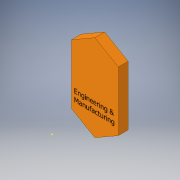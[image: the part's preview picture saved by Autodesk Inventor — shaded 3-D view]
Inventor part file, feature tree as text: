
AUTODESK INVENTOR PART (.ipt)
format: ipt  version: 2018 (Build 220112000, 112)  size: 98,304 bytes
history: native  units: in
note: dims shown in document units (in); Inventor stores cm internally (conversion verified against a paired STEP export)
features: sketch x2, extrude x1
ambient origin geometry x8: Origin, YZ Plane, XZ Plane, XY Plane, X Axis, Y Axis, Z Axis, Center Point
bodies: Solid1 (feature_tree)
feature tree (3):
  extrude  "Extrusion1"  [1 undecoded]
  sketch  "Sketch2"
  sketch  "Sketch1"  dims[d2=1.108in d3=0.6in d4=0.125in d5=0.0in]
note: 1 required parameter value undecoded (feature->parameter linkage not recoverable at this tier; creation-order binding heuristic only, values carry confidence <= 0.55)
